# Revit family: HERZ Diaphragm Pressure Reducing Valve With Brass Cap 2682
name_source: partatom
category: Rohrzubehör
revit_build: Autodesk Revit 2018 (Build: 20190510_1515(x64)
units: mm (PartAtom-declared; Revit-internal decimal feet)

## family parameters
Arbeitsebenenbasiert = Nein
Beim Laden mit Abzugskörper schneiden = Nein
Bemaßung runder Anschluss = Durchmesser verwenden
Gemeinsam genutzt = Nein
Immer vertikal = Ja
OmniClass-Nummer = 23.65.55.14
OmniClass-Titel = Valves for Liquid Services
Teiletyp = Unterbricht

## types (2) — shared parameters
Application = The pressure reducing valve protects installations against over pressure (reduces input pressure to a working level).
It can also be used in heating systems to protect boiler against increased pressure.
The outlet pressure is adjustable and does not vary with changes of the inlet pressure.
The outlet pressure can be adjusted by turning the green handle.
Turning the handle clockwise increases the outlet pressure.
Turning above the stated values on the pressure reducer scale may damage the valve.
We recommend the max. outlet pressure of 4 bar for private house installations (product long life, costs,...).
After each new setting of the outlet pressure, the regulated pipe has to be opened and closed.
B02 = 26 mm  [stored 0.0853018 ft]
B03 = 5 mm  [stored 0.0164042 ft]
Body = forged brass acc. to EN 12165; CW626N
Bottom cover = brass CW626N
Diaphragm = EPDM
External thread = acc. to ISO 7-1 and ISO228
Factory settings = 300000.0 Pa
Filter = stainless steel, mesh size 0.3 mm
Handle = PA 6.6, green
Hersteller = HERZ Armaturen Ges.m.b.H.
Manometer scale = 0 - 10 bar
Max. inlet pressure = 1600000.0 Pa
Max. operating temperature = 70 °C
Medium = water
Note = Pursuant to Article 33 of the REACH Regulation (EC No. 1907/2006), we are obliged to point out that the material lead is listed on the SVHC list and that all brass components manufactured in our products exceed 0.1% (w / w) lead (CAS: 7439-92-1 / EINECS: 231-100-4).
Since lead is a component part of an alloy, actual exposure is not possible and therefore no additional information on safe use is necessary.
Outlet pressure range = 1.5 - 6 bar
Pressure gauge connectors = 1/4" F (ISO 228-1)
R06 = 19.5 mm  [stored 0.0639764 ft]
S02 = 10 mm  [stored 0.0328084 ft]
SCTWCODE = 04;24;02
SCTWSEQ = AW;SBT_TYP_AW="111";2
Sealing = EPDM
Spring = spring steel
Spring guide = stainless steel
Standard = EN 1567
URL = www.herzvalves.com
Upper part = PA6.6
W01 = 91.00°
zero-valued in all types: SC_NennweiteBerechnet

## type names (no varying parameters)
- Manometer front
- Manometer back

note: [stored X ft] marks values corroborated as IEEE doubles in the binary element streams (Revit-internal decimal feet)
